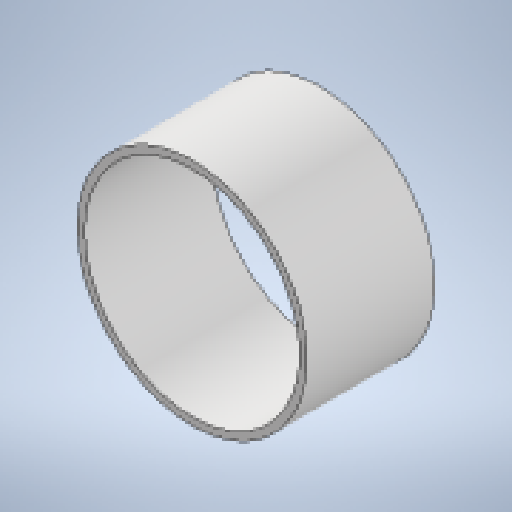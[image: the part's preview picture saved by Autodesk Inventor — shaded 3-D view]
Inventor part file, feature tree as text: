
AUTODESK INVENTOR PART (.ipt)
format: ipt  version: 2025.1 (Build 291241020, 241B)  size: 143,872 bytes
history: native  units: mm
features: extrude x1, sketch x1
ambient origin geometry x8: Origin, YZ Plane, XZ Plane, XY Plane, X Axis, Y Axis, Z Axis, Center Point
bodies: Solid1 (feature_tree)
feature tree (2):
  extrude  "Extrusion1"  Depth=50.0mm
  sketch  "Sketch1"  dims[d0=90.0mm d1=3.0mm d2=50.0mm d3=0.0mm]
